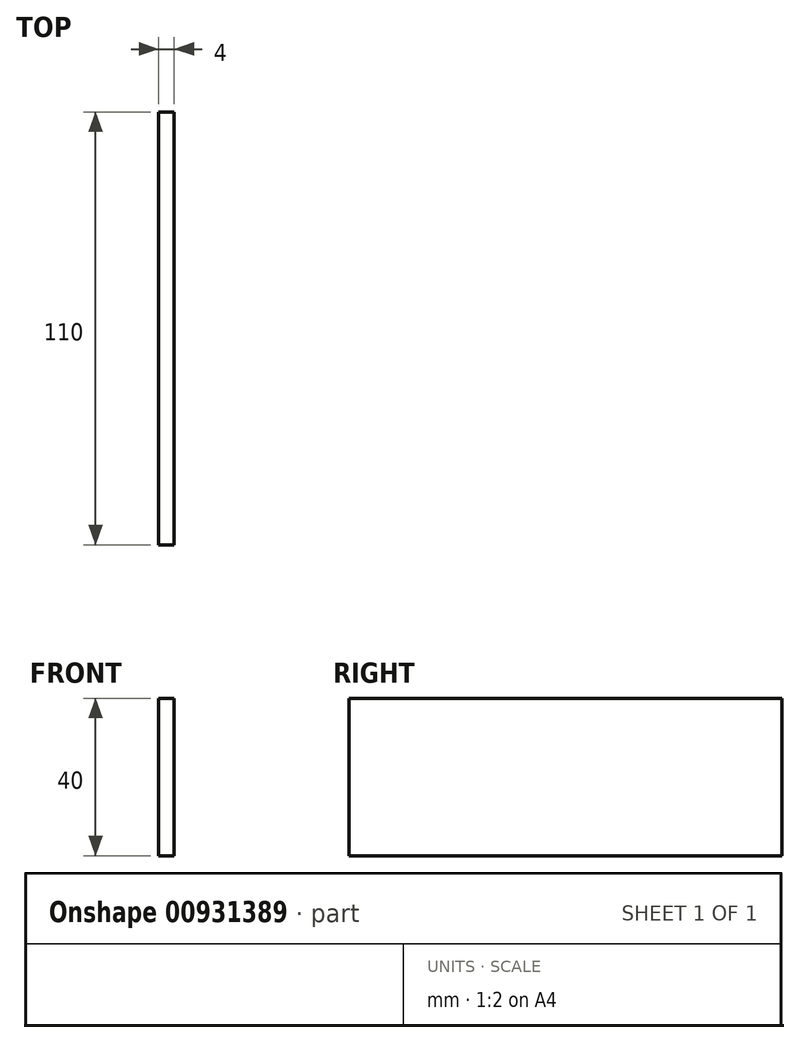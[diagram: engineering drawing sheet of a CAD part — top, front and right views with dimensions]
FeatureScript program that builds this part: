
annotation { "Feature Type Name" : "Feature", "Feature Type Description" : "" }
export const myFeature = defineFeature(function(context is Context, id is Id, definition is map)
    precondition{}
    {
        {
            var Q0;
            Q0=qCreatedBy(makeId("Right.planeOp"),FACE);
            cPlane(context, id + "F0", {"entities" : qUnion([Q0]), "cplaneType" : CPlaneType.OFFSET, "offset" : 100 * mm, "width" : 150 * mm, "height" : 150 * mm});
        }
        {
            var Q0;
            Q0=qCreatedBy(id+"F0.planeOp",FACE);
            var sketch = newSketch(context, id + "F1", { "sketchPlane" : qUnion([Q0])});
            skLineSegment(sketch, "E0.bottom", {"start": v(55, -20) * mm, "end": v(-55, -20) * mm});
            skLineSegment(sketch, "E0.top", {"start": v(55, 20) * mm, "end": v(-55, 20) * mm});
            skLineSegment(sketch, "E0.left", {"start": v(55, -20) * mm, "end": v(55, 20) * mm});
            skLineSegment(sketch, "E0.right", {"start": v(-55, -20) * mm, "end": v(-55, 20) * mm});
            skPoint(sketch, "E0.middle", {"position": v(0, 0) * mm});
            skSolve(sketch);
        }
        {
            var Q0;
            Q0 = qSketchRegion(id + "F1", true);
            var Q1;
            Q1=makeQuery(id+"F1.imprint","IMPRINT",FACE,{"disambiguationData":[TD([[makeQuery(id+"F1.imprint","IMPRINT",EDGE,{"derivedFrom":sQuery(id+"F1.wireOp",EDGE,"E0.bottom")}),-1.0]])]});
            extrude(context, id + "F2", {"entities" : qUnion([Q0, Q1]), "depth" : 4 * mm, "offsetDistance" : 25 * mm});
        }
    });
